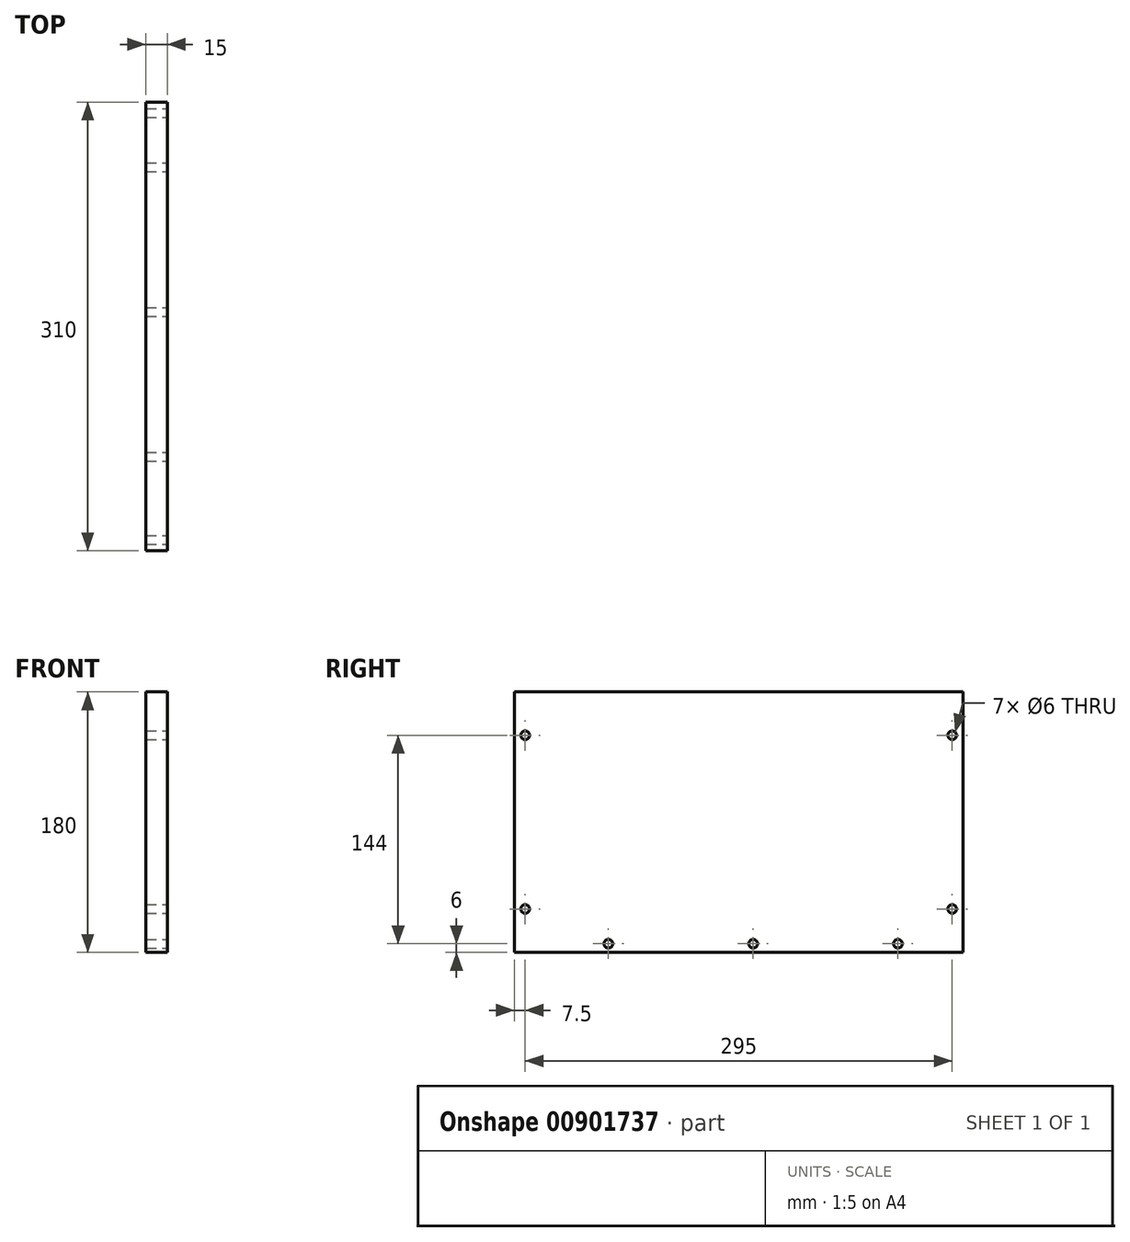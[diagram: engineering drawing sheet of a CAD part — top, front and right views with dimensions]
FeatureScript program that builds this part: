
annotation { "Feature Type Name" : "Feature", "Feature Type Description" : "" }
export const myFeature = defineFeature(function(context is Context, id is Id, definition is map)
    precondition{}
    {
        {
            var Q0;
            Q0=qCreatedBy(makeId("Right.planeOp"),FACE);
            var sketch = newSketch(context, id + "F0", { "sketchPlane" : qUnion([Q0])});
            skLineSegment(sketch, "E0.bottom", {"start": v(0, 0) * mm, "end": v(310, 0) * mm});
            skLineSegment(sketch, "E0.top", {"start": v(0, 180) * mm, "end": v(310, 180) * mm});
            skLineSegment(sketch, "E0.left", {"start": v(0, 0) * mm, "end": v(0, 180) * mm});
            skLineSegment(sketch, "E0.right", {"start": v(310, 0) * mm, "end": v(310, 180) * mm});
            skSolve(sketch);
        }
        {
            var Q0;
            Q0=makeQuery(id+"F0.imprint","IMPRINT",FACE,{"disambiguationData":[TD([[makeQuery(id+"F0.imprint","IMPRINT",EDGE,{"derivedFrom":sQuery(id+"F0.wireOp",EDGE,"E0.bottom")}),1.0]])]});
            extrude(context, id + "F1", {"entities" : qUnion([Q0]), "depth" : 15 * mm, "offsetDistance" : 25 * mm});
        }
        {
            var Q0;
            Q0=makeQuery(id+"F1.opExtrude","CAP_FACE",FACE,{"disambiguationData":[OSD([sQuery(id+"F0.wireOp",EDGE,"E0.bottom"),sQuery(id+"F0.wireOp",EDGE,"E0.top"),sQuery(id+"F0.wireOp",EDGE,"E0.left"),sQuery(id+"F0.wireOp",EDGE,"E0.right")])],"isStart":false});
            var sketch = newSketch(context, id + "F2", { "sketchPlane" : qUnion([Q0])});
            skCircle(sketch, "E1", {"center": v(7.5, 30) * mm, "radius": 3 * mm});
            skCircle(sketch, "E2", {"center": v(7.5, 150) * mm, "radius": 3 * mm});
            skCircle(sketch, "E3", {"center": v(302.5, 150) * mm, "radius": 3 * mm});
            skCircle(sketch, "E4", {"center": v(302.5, 30) * mm, "radius": 3 * mm});
            skCircle(sketch, "E5", {"center": v(65, 6) * mm, "radius": 3 * mm});
            skCircle(sketch, "E6", {"center": v(165, 6) * mm, "radius": 3 * mm});
            skCircle(sketch, "E7", {"center": v(265, 6) * mm, "radius": 3 * mm});
            skSolve(sketch);
        }
        {
            var Q0;
            Q0 = qSketchRegion(id + "F2", true);
            extrude(context, id + "F3", {"entities" : qUnion([Q0]), "operationType" : NewBodyOperationType.REMOVE, "endBound" : BoundingType.THROUGH_ALL, "oppositeDirection" : true, "depth" : 25 * mm, "offsetDistance" : 25 * mm});
        }
    });
